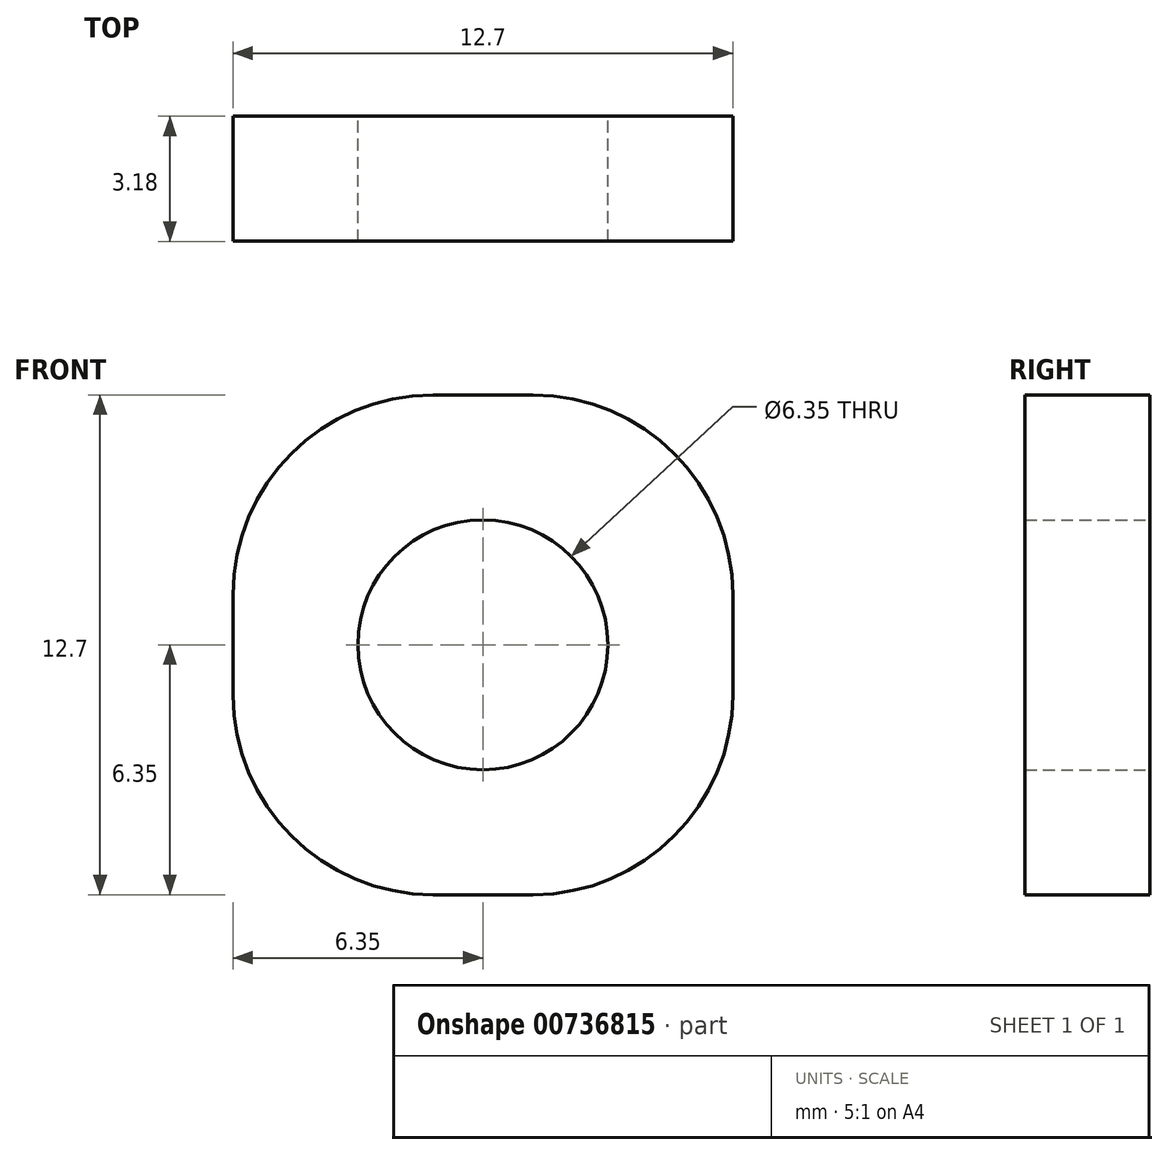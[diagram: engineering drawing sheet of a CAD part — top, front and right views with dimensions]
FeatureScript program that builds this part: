
annotation { "Feature Type Name" : "Feature", "Feature Type Description" : "" }
export const myFeature = defineFeature(function(context is Context, id is Id, definition is map)
    precondition{}
    {
        {
            var Q0;
            Q0=qCreatedBy(makeId("Front.planeOp"),FACE);
            var sketch = newSketch(context, id + "F0", { "sketchPlane" : qUnion([Q0])});
            skLineSegment(sketch, "E0.bottom", {"start": v(0, 0) * mm, "end": v(-12.7, 0) * mm});
            skLineSegment(sketch, "E0.top", {"start": v(0, 12.7) * mm, "end": v(-12.7, 12.7) * mm});
            skLineSegment(sketch, "E0.left", {"start": v(0, 0) * mm, "end": v(0, 12.7) * mm});
            skLineSegment(sketch, "E0.right", {"start": v(-12.7, 0) * mm, "end": v(-12.7, 12.7) * mm});
            skLineSegment(sketch, "E1", {"start": v(-6.35, 0) * mm, "end": v(-6.35, 12.7) * mm});
            skCircle(sketch, "E2", {"center": v(-6.35, 6.35) * mm, "radius": 3.18 * mm});
            skSolve(sketch);
        }
        {
            var Q0;
            {var subQ0=sQuery(id+"F0.wireOp",EDGE,"E0.right");Q0=makeQuery(id+"F0.imprint","IMPRINT",FACE,{"disambiguationData":[TD([[makeQuery(id+"F0.imprint","IMPRINT",EDGE,{"derivedFrom":subQ0}),-1.0]])]});}
            var Q1;
            {var subQ5=sQuery(id+"F0.wireOp",EDGE,"E0.left");Q1=makeQuery(id+"F0.imprint","IMPRINT",FACE,{"disambiguationData":[TD([[makeQuery(id+"F0.imprint","IMPRINT",EDGE,{"derivedFrom":subQ5}),1.0]])]});}
            extrude(context, id + "F1", {"entities" : qUnion([Q0, Q1]), "depth" : 3.17 * mm, "offsetDistance" : 25.4 * mm});
        }
        {
            var Q0;
            Q0=makeQuery(id+"F1.opExtrude","SWEPT_EDGE",EDGE,{"disambiguationData":[OSD([sQuery(id+"F0.wireOp",EDGE,"E0.bottom"),sQuery(id+"F0.wireOp",EDGE,"E0.right")])]});
            fillet(context, id + "F2", {"entities" : qUnion([Q0]), "radius" : 5.08 * mm, "tangentPropagation" : true, "allowEdgeOverflow" : false});
        }
        {
            var Q0;
            Q0=makeQuery(id+"F1.opExtrude","SWEPT_EDGE",EDGE,{"disambiguationData":[OSD([sQuery(id+"F0.wireOp",EDGE,"E0.bottom"),sQuery(id+"F0.wireOp",EDGE,"E0.left")])]});
            fillet(context, id + "F3", {"entities" : qUnion([Q0]), "radius" : 5.08 * mm, "tangentPropagation" : true, "allowEdgeOverflow" : false});
        }
        {
            var Q0;
            Q0=makeQuery(id+"F1.opExtrude","SWEPT_EDGE",EDGE,{"disambiguationData":[OSD([sQuery(id+"F0.wireOp",EDGE,"E0.top"),sQuery(id+"F0.wireOp",EDGE,"E0.left")])]});
            fillet(context, id + "F4", {"entities" : qUnion([Q0]), "radius" : 5.08 * mm, "tangentPropagation" : true, "allowEdgeOverflow" : false});
        }
        {
            var Q0;
            Q0=makeQuery(id+"F1.opExtrude","SWEPT_EDGE",EDGE,{"disambiguationData":[OSD([sQuery(id+"F0.wireOp",EDGE,"E0.top"),sQuery(id+"F0.wireOp",EDGE,"E0.right")])]});
            fillet(context, id + "F5", {"entities" : qUnion([Q0]), "radius" : 5.08 * mm, "tangentPropagation" : true, "allowEdgeOverflow" : false});
        }
    });
